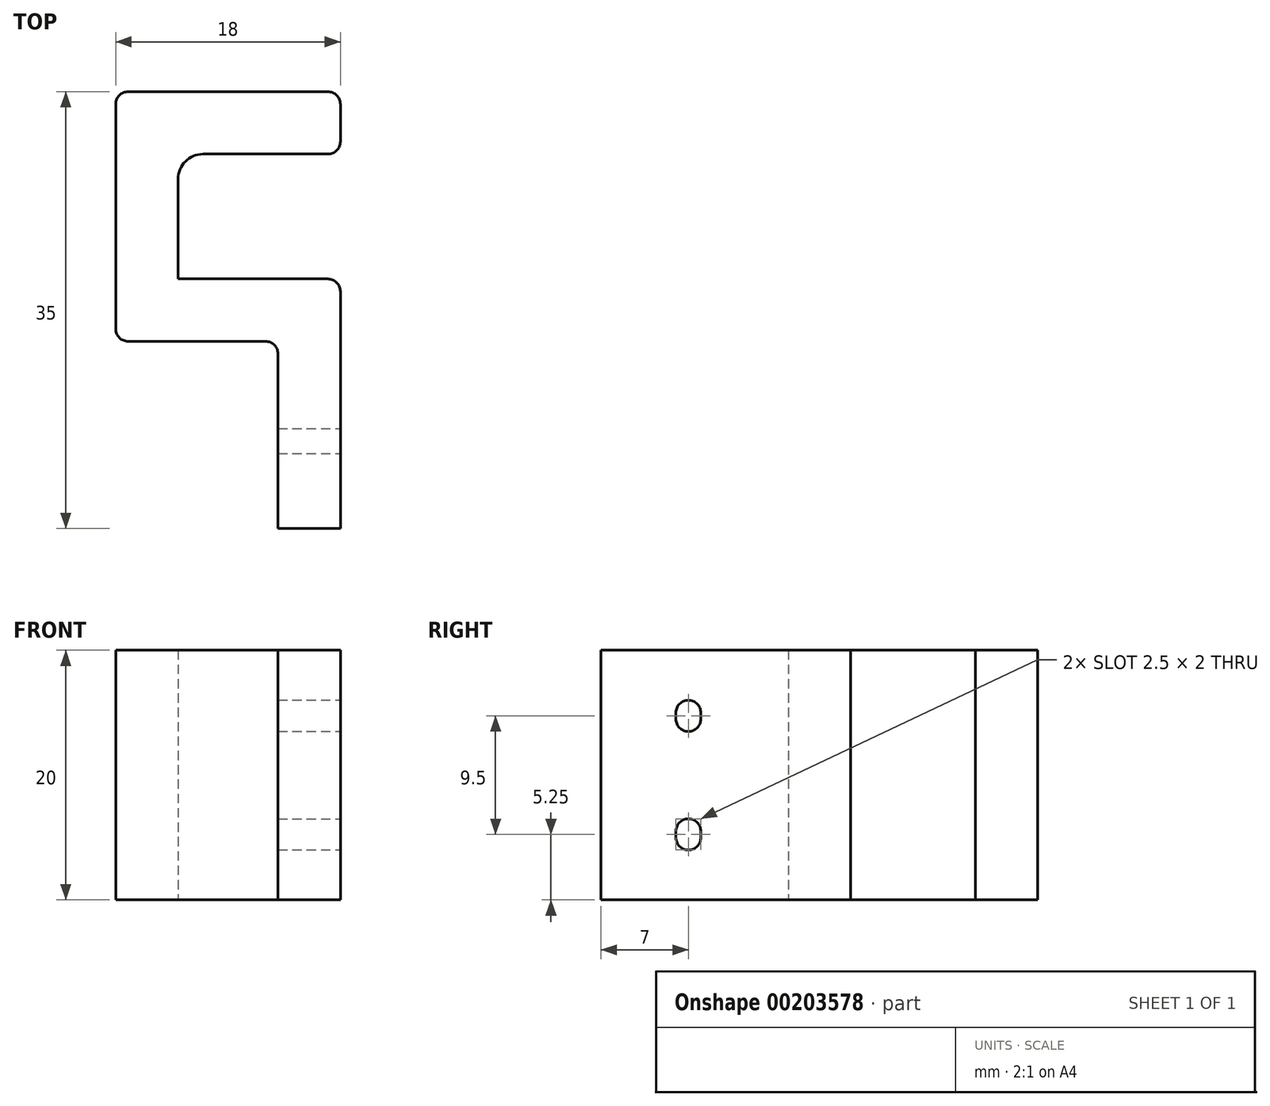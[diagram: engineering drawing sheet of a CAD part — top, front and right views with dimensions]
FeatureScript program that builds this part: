
annotation { "Feature Type Name" : "Feature", "Feature Type Description" : "" }
export const myFeature = defineFeature(function(context is Context, id is Id, definition is map)
    precondition{}
    {
        {
            var Q0;
            Q0=qCreatedBy(makeId("Top.planeOp"),FACE);
            var sketch = newSketch(context, id + "F0", { "sketchPlane" : qUnion([Q0])});
            skLineSegment(sketch, "E0", {"start": v(0, 0) * mm, "end": v(0, 19) * mm});
            skLineSegment(sketch, "E1", {"start": v(-1, 20) * mm, "end": v(-13, 20) * mm});
            skLineSegment(sketch, "E2", {"start": v(-13, 20) * mm, "end": v(-13, 28) * mm});
            skLineSegment(sketch, "E3", {"start": v(-11, 30) * mm, "end": v(-1, 30) * mm});
            skLineSegment(sketch, "E4", {"start": v(0, 31) * mm, "end": v(0, 34) * mm});
            skLineSegment(sketch, "E5", {"start": v(-1, 35) * mm, "end": v(-17, 35) * mm});
            skLineSegment(sketch, "E6", {"start": v(-18, 34) * mm, "end": v(-18, 16) * mm});
            skLineSegment(sketch, "E7", {"start": v(-17, 15) * mm, "end": v(-6, 15) * mm});
            skLineSegment(sketch, "E8", {"start": v(-5, 14) * mm, "end": v(-5, 0) * mm});
            skLineSegment(sketch, "E9", {"start": v(-5, 0) * mm, "end": v(0, 0) * mm});
            skPoint(sketch, "E10.visualSharp", {"position": v(-13, 30) * mm});
            skArc(sketch, "E10.filletArc", {"start": v(-11, 30) * mm, "mid": v(-12.41, 29.41) * mm, "end": v(-13, 28) * mm});
            skPoint(sketch, "E11.visualSharp", {"position": v(0, 30) * mm});
            skArc(sketch, "E11.filletArc", {"start": v(-1, 30) * mm, "mid": v(-0.3, 30.3) * mm, "end": v(0, 31) * mm});
            skPoint(sketch, "E12.visualSharp", {"position": v(0, 20) * mm});
            skArc(sketch, "E12.filletArc", {"start": v(0, 19) * mm, "mid": v(-0.3, 19.7) * mm, "end": v(-1, 20) * mm});
            skPoint(sketch, "E13.visualSharp", {"position": v(-5, 15) * mm});
            skArc(sketch, "E13.filletArc", {"start": v(-5, 14) * mm, "mid": v(-5.3, 14.7) * mm, "end": v(-6, 15) * mm});
            skPoint(sketch, "E14.visualSharp", {"position": v(-18, 15) * mm});
            skArc(sketch, "E14.filletArc", {"start": v(-18, 16) * mm, "mid": v(-17.7, 15.3) * mm, "end": v(-17, 15) * mm});
            skPoint(sketch, "E15.visualSharp", {"position": v(-18, 35) * mm});
            skArc(sketch, "E15.filletArc", {"start": v(-17, 35) * mm, "mid": v(-17.7, 34.7) * mm, "end": v(-18, 34) * mm});
            skPoint(sketch, "E16.visualSharp", {"position": v(0, 35) * mm});
            skArc(sketch, "E16.filletArc", {"start": v(0, 34) * mm, "mid": v(-0.3, 34.7) * mm, "end": v(-1, 35) * mm});
            skSolve(sketch);
        }
        {
            var Q0;
            Q0=makeQuery(id+"F0.imprint","IMPRINT",FACE,{"disambiguationData":[TD([[makeQuery(id+"F0.imprint","IMPRINT",EDGE,{"derivedFrom":sQuery(id+"F0.wireOp",EDGE,"E0")}),1.0]])]});
            extrude(context, id + "F1", {"entities" : qUnion([Q0]), "depth" : 20 * mm});
        }
        {
            var Q0;
            Q0=makeQuery(id+"F1.opExtrude","SWEPT_FACE",FACE,{"disambiguationData":[OSD([sQuery(id+"F0.wireOp",EDGE,"E0")])]});
            var sketch = newSketch(context, id + "F2", { "sketchPlane" : qUnion([Q0])});
            skLineSegment(sketch, "E17.bottom", {"start": v(7, 16) * mm, "end": v(7, 16) * mm});
            skLineSegment(sketch, "E17.top", {"start": v(7, 13.5) * mm, "end": v(7, 13.5) * mm});
            skLineSegment(sketch, "E17.left", {"start": v(6, 15) * mm, "end": v(6, 14.5) * mm});
            skLineSegment(sketch, "E17.right", {"start": v(8, 15) * mm, "end": v(8, 14.5) * mm});
            skLineSegment(sketch, "E18.1.0.0", {"start": v(7, 6.5) * mm, "end": v(7, 6.5) * mm});
            skLineSegment(sketch, "E18.1.0.1", {"start": v(7, 4) * mm, "end": v(7, 4) * mm});
            skLineSegment(sketch, "E18.1.0.2", {"start": v(6, 5.5) * mm, "end": v(6, 5) * mm});
            skLineSegment(sketch, "E18.1.0.3", {"start": v(8, 5.5) * mm, "end": v(8, 5) * mm});
            skLineSegment(sketch, "E18.direction1", {"start": v(6, 13.5) * mm, "end": v(6, 4) * mm, "construction": true});
            skPoint(sketch, "E19.visualSharp", {"position": v(6, 16) * mm});
            skArc(sketch, "E19.filletArc", {"start": v(7, 16) * mm, "mid": v(6.3, 15.7) * mm, "end": v(6, 15) * mm});
            skPoint(sketch, "E20.visualSharp", {"position": v(8, 16) * mm});
            skArc(sketch, "E20.filletArc", {"start": v(8, 15) * mm, "mid": v(7.7, 15.7) * mm, "end": v(7, 16) * mm});
            skPoint(sketch, "E21.visualSharp", {"position": v(6, 13.5) * mm});
            skArc(sketch, "E21.filletArc", {"start": v(6, 14.5) * mm, "mid": v(6.3, 13.8) * mm, "end": v(7, 13.5) * mm});
            skPoint(sketch, "E22.visualSharp", {"position": v(8, 13.5) * mm});
            skArc(sketch, "E22.filletArc", {"start": v(7, 13.5) * mm, "mid": v(7.7, 13.8) * mm, "end": v(8, 14.5) * mm});
            skPoint(sketch, "E23.visualSharp", {"position": v(6, 6.5) * mm});
            skArc(sketch, "E23.filletArc", {"start": v(7, 6.5) * mm, "mid": v(6.3, 6.2) * mm, "end": v(6, 5.5) * mm});
            skPoint(sketch, "E24.visualSharp", {"position": v(8, 6.5) * mm});
            skArc(sketch, "E24.filletArc", {"start": v(8, 5.5) * mm, "mid": v(7.7, 6.2) * mm, "end": v(7, 6.5) * mm});
            skPoint(sketch, "E25.visualSharp", {"position": v(8, 4) * mm});
            skArc(sketch, "E25.filletArc", {"start": v(7, 4) * mm, "mid": v(7.7, 4.3) * mm, "end": v(8, 5) * mm});
            skPoint(sketch, "E26.visualSharp", {"position": v(6, 4) * mm});
            skArc(sketch, "E26.filletArc", {"start": v(6, 5) * mm, "mid": v(6.3, 4.3) * mm, "end": v(7, 4) * mm});
            skSolve(sketch);
        }
        {
            var Q0;
            Q0 = qSketchRegion(id + "F2", true);
            extrude(context, id + "F3", {"entities" : qUnion([Q0]), "operationType" : NewBodyOperationType.REMOVE, "endBound" : BoundingType.THROUGH_ALL, "oppositeDirection" : true, "depth" : 25 * mm});
        }
    });
